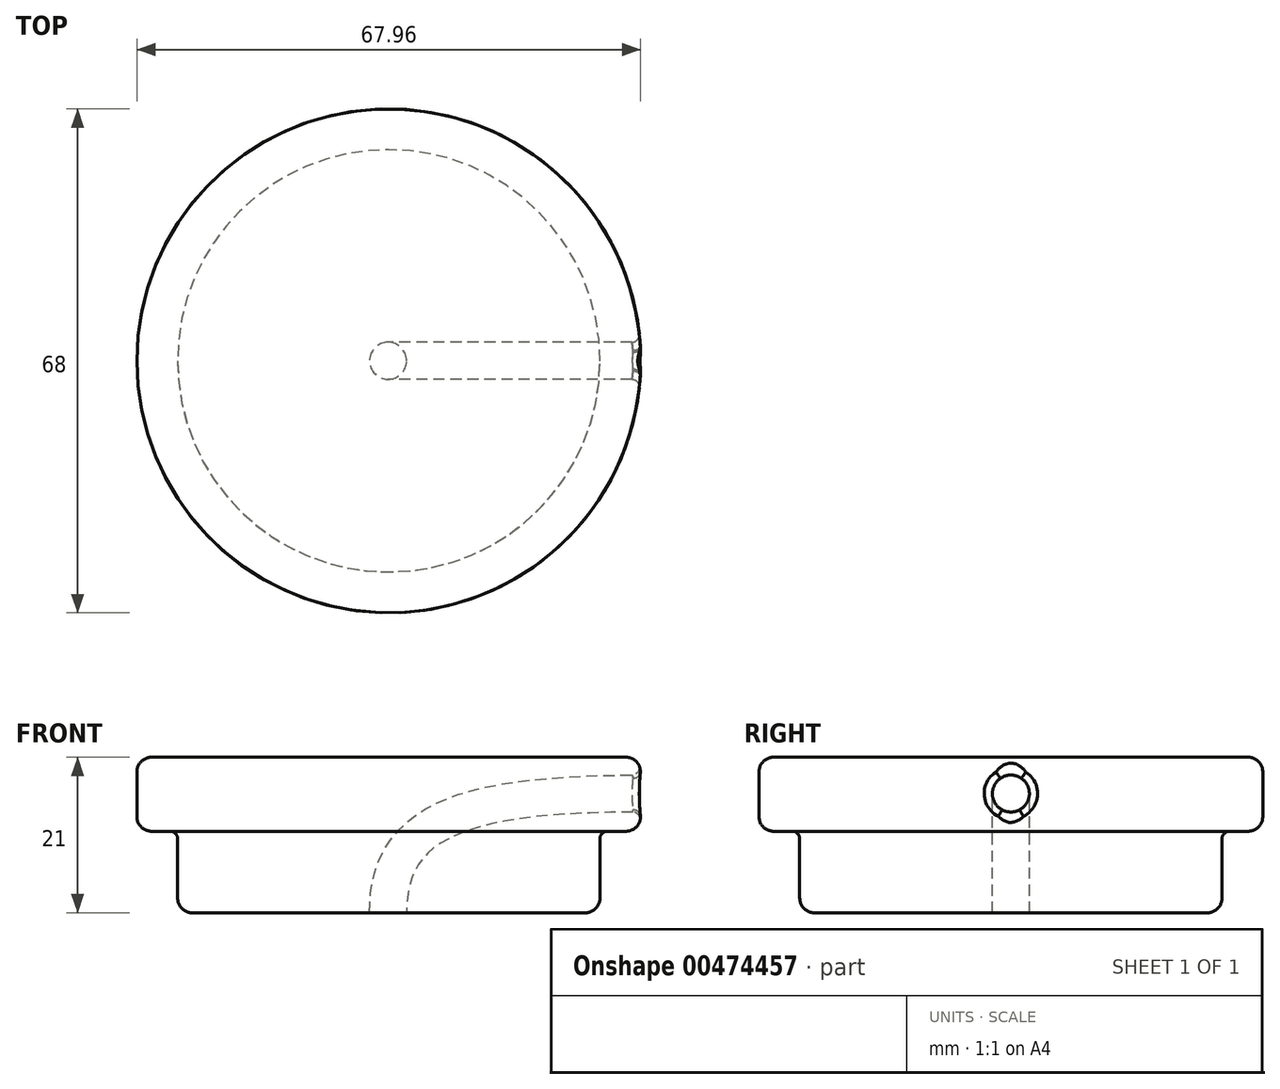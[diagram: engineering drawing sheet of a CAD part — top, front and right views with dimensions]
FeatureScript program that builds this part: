
annotation { "Feature Type Name" : "Feature", "Feature Type Description" : "" }
export const myFeature = defineFeature(function(context is Context, id is Id, definition is map)
    precondition{}
    {
        {
            var Q0;
            Q0=qCreatedBy(makeId("Front.planeOp"),FACE);
            var sketch = newSketch(context, id + "F0", { "sketchPlane" : qUnion([Q0])});
            skLineSegment(sketch, "E0", {"start": v(0, 12.98) * mm, "end": v(0, -13.64) * mm, "construction": true});
            skLineSegment(sketch, "E1", {"start": v(0, 0) * mm, "end": v(0, 10) * mm});
            skLineSegment(sketch, "E2", {"start": v(0, 10) * mm, "end": v(34, 10) * mm});
            skLineSegment(sketch, "E3", {"start": v(34, 10) * mm, "end": v(34, 0) * mm});
            skLineSegment(sketch, "E4", {"start": v(34, 0) * mm, "end": v(28.5, 0) * mm});
            skLineSegment(sketch, "E5", {"start": v(28.5, 0) * mm, "end": v(28.5, -11) * mm});
            skLineSegment(sketch, "E6", {"start": v(28.5, -11) * mm, "end": v(0, -11) * mm});
            skLineSegment(sketch, "E7", {"start": v(0, -11) * mm, "end": v(0, 0) * mm});
            skArc(sketch, "E8", {"start": v(26.5, -11) * mm, "mid": v(27.91, -10.41) * mm, "end": v(28.5, -9) * mm});
            skSolve(sketch);
        }
        {
            var Q0;
            Q0=makeQuery(id+"F0.imprint","IMPRINT",FACE,{"disambiguationData":[TD([[makeQuery(id+"F0.imprint","IMPRINT",EDGE,{"derivedFrom":sQuery(id+"F0.wireOp",EDGE,"E1")}),-1.0]])]});
            var sketch = newSketch(context, id + "F1", { "sketchPlane" : qUnion([Q0])});
            skLineSegment(sketch, "E9", {"start": v(34, 10) * mm, "end": v(34, 0) * mm, "construction": true});
            skFitSpline(sketch, "E10", {"points": [v(34, 5) * mm, v(0, -11) * mm], "startDerivative": vector(-73.33, 0) * mm, "endDerivative": vector(0, -36.49) * mm});
            skSolve(sketch);
        }
        {
            var Q0;
            Q0=sQuery(id+"F1.wireOp",VERTEX,"E10.0.internal");
            var Q1;
            Q1=qCreatedBy(makeId("Right.planeOp"),FACE);
            cPlane(context, id + "F2", {"entities" : qUnion([Q0, Q1]), "cplaneType" : CPlaneType.PLANE_POINT, "offset" : 25 * mm, "width" : 150 * mm, "height" : 150 * mm});
        }
        {
            var Q0;
            Q0=qCreatedBy(id+"F2.planeOp",FACE);
            var sketch = newSketch(context, id + "F3", { "sketchPlane" : qUnion([Q0])});
            skLineSegment(sketch, "E11", {"start": v(0, 10.2) * mm, "end": v(0, 0) * mm, "construction": true});
            skCircle(sketch, "E12", {"center": v(0, 5.1) * mm, "radius": 2.5 * mm});
            skSolve(sketch);
        }
        {
            var Q0;
            Q0=makeQuery(id+"F0.imprint","IMPRINT",FACE,{"disambiguationData":[TD([[makeQuery(id+"F0.imprint","IMPRINT",EDGE,{"derivedFrom":sQuery(id+"F0.wireOp",EDGE,"E1")}),-1.0]])]});
            var Q1;
            Q1=sQuery(id+"F0.wireOp",EDGE,"E0");
            revolve(context, id + "F4", {"entities" : qUnion([Q0]), "axis" : qUnion([Q1]), "revolveType" : RevolveType.FULL});
        }
        {
            var Q0;
            Q0=makeQuery(id+"F3.imprint","IMPRINT",FACE,{"disambiguationData":[TD([[makeQuery(id+"F3.imprint","IMPRINT",EDGE,{"derivedFrom":sQuery(id+"F3.wireOp",EDGE,"E12")}),1.0]])]});
            var Q1;
            Q1=sQuery(id+"F1.wireOp",EDGE,"E10");
            sweep(context, id + "F5", {"operationType" : NewBodyOperationType.REMOVE, "profiles" : qUnion([Q0]), "path" : qUnion([Q1])});
        }
        {
            var Q0;
            Q0=makeQuery(id+"F4.opRevolve","SWEPT_EDGE",EDGE,{"disambiguationData":[OSD([sQuery(id+"F0.wireOp",EDGE,"E2"),sQuery(id+"F0.wireOp",EDGE,"E3")])]});
            var Q1;
            Q1=makeQuery(id+"F4.opRevolve","SWEPT_EDGE",EDGE,{"disambiguationData":[OSD([sQuery(id+"F0.wireOp",EDGE,"E3"),sQuery(id+"F0.wireOp",EDGE,"E4")])]});
            fillet(context, id + "F6", {"entities" : qUnion([Q0, Q1]), "radius" : 2 * mm, "tangentPropagation" : true, "allowEdgeOverflow" : false});
        }
        {
            var Q0;
            Q0=makeQuery(id+"F4.opRevolve","SWEPT_EDGE",EDGE,{"disambiguationData":[OSD([sQuery(id+"F0.wireOp",EDGE,"E4"),sQuery(id+"F0.wireOp",EDGE,"E5")])]});
            var Q1;
            Q1=makeQuery(id+"F5.boolean.opBoolean","INTERSECT",EDGE,{"derivedFrom":[makeQuery(id+"F4.opRevolve","SWEPT_FACE",FACE,{"disambiguationData":[OSD([sQuery(id+"F0.wireOp",EDGE,"E3")])]}),makeQuery(id+"F5.opSweep","SWEPT_FACE",FACE,{"disambiguationData":[OSD([sQuery(id+"F1.wireOp",EDGE,"E10"),sQuery(id+"F3.wireOp",EDGE,"E12")])]})]});
            var Q2;
            Q2=makeQuery(id+"F5.boolean.opBoolean","COPY",EDGE,{"derivedFrom":makeQuery(id+"F5.opSweep","CAP_EDGE",EDGE,{"disambiguationData":[OSD([sQuery(id+"F1.wireOp",VERTEX,"E10.end"),sQuery(id+"F3.wireOp",EDGE,"E12")])],"isStart":false})});
            fillet(context, id + "F7", {"entities" : qUnion([Q0, Q1, Q2]), "radius" : 1 * mm, "tangentPropagation" : true, "allowEdgeOverflow" : false});
        }
    });
